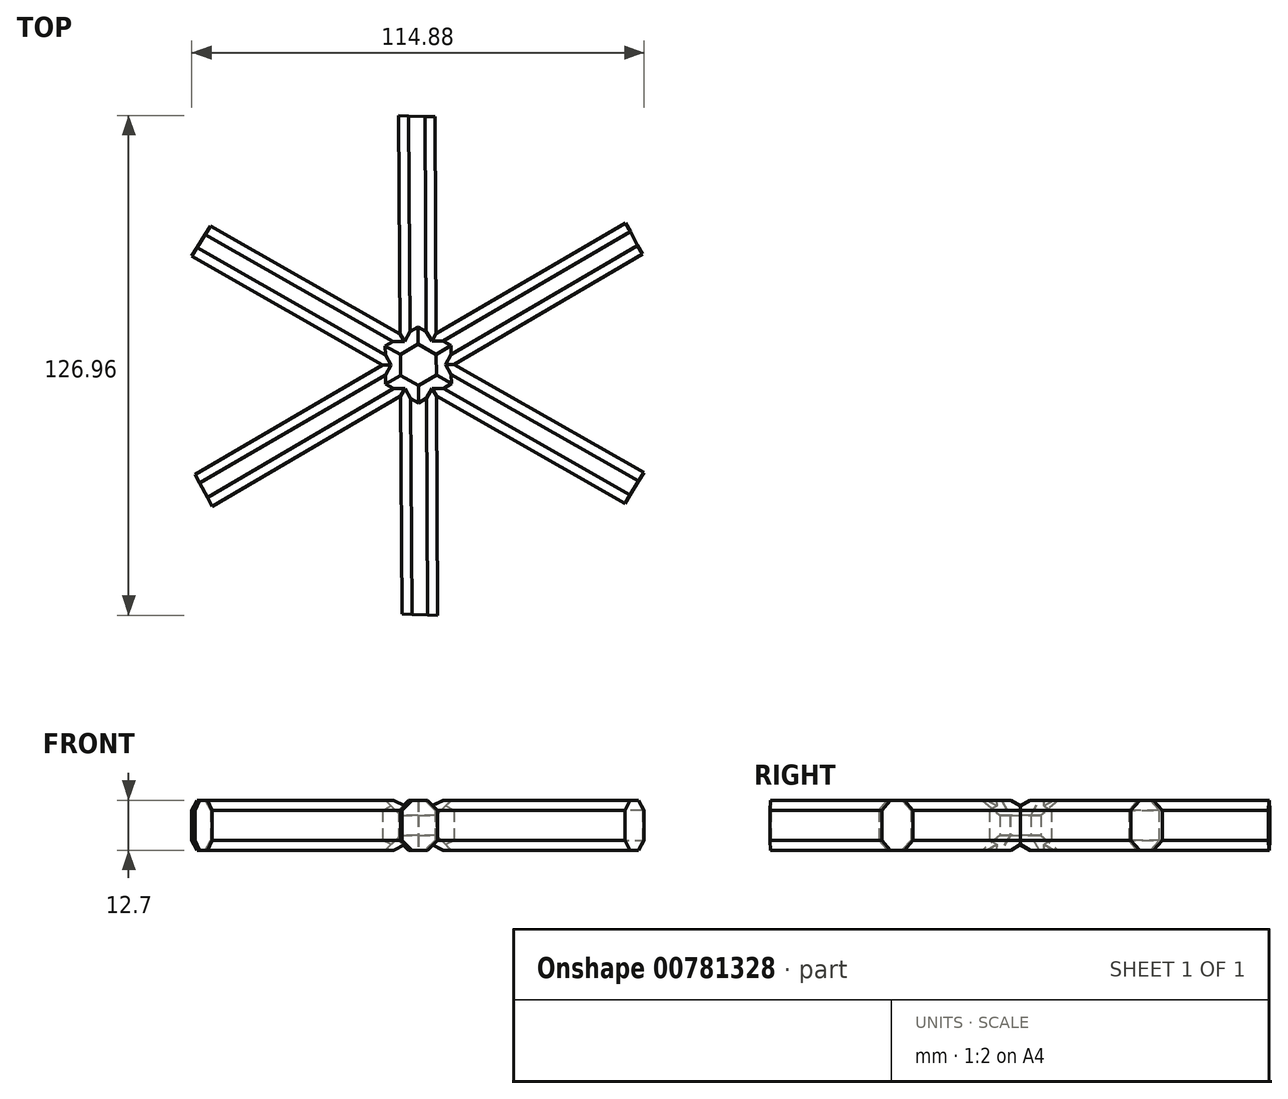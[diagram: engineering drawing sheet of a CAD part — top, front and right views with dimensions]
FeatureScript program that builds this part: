
annotation { "Feature Type Name" : "Feature", "Feature Type Description" : "" }
export const myFeature = defineFeature(function(context is Context, id is Id, definition is map)
    precondition{}
    {
        {
            var Q0;
            Q0=qCreatedBy(makeId("Top.planeOp"),FACE);
            var sketch = newSketch(context, id + "F0", { "sketchPlane" : qUnion([Q0])});
            skPoint(sketch, "E0.center", {"position": v(0, 0) * mm});
            skLineSegment(sketch, "E1", {"start": v(-5, 63.32) * mm, "end": v(-4.1, -63.34) * mm});
            skLineSegment(sketch, "E2", {"start": v(4.25, 63.02) * mm, "end": v(4.87, -63.64) * mm});
            skLineSegment(sketch, "E3.1.2", {"start": v(-52.34, -35.98) * mm, "end": v(56.9, 28.12) * mm});
            skLineSegment(sketch, "E3.1.3", {"start": v(-56.7, -27.83) * mm, "end": v(52.68, 36.04) * mm});
            skLineSegment(sketch, "E3.2.2", {"start": v(57.33, -27.33) * mm, "end": v(-52.8, 35.22) * mm});
            skLineSegment(sketch, "E3.2.3", {"start": v(52.45, -35.2) * mm, "end": v(-57.55, 27.6) * mm});
            skLineSegment(sketch, "E4", {"start": v(4.25, 63.02) * mm, "end": v(-5, 63.32) * mm});
            skLineSegment(sketch, "E5", {"start": v(-52.8, 35.22) * mm, "end": v(-57.55, 27.6) * mm});
            skLineSegment(sketch, "E6", {"start": v(-52.34, -35.98) * mm, "end": v(-56.7, -27.83) * mm});
            skLineSegment(sketch, "E7", {"start": v(-4.1, -63.34) * mm, "end": v(4.87, -63.64) * mm});
            skLineSegment(sketch, "E8", {"start": v(52.45, -35.2) * mm, "end": v(57.33, -27.33) * mm});
            skLineSegment(sketch, "E9", {"start": v(56.9, 28.12) * mm, "end": v(52.68, 36.04) * mm});
            skSolve(sketch);
        }
        {
            var Q0;
            Q0 = qSketchRegion(id + "F0", true);
            extrude(context, id + "F1", {"entities" : qUnion([Q0]), "depth" : 12.7 * mm, "offsetDistance" : 25.4 * mm});
        }
        {
            var Q0;
            {var subQ0=sQuery(id+"F0.wireOp",EDGE,"E3.1.2");Q0=makeQuery(id+"F1.opExtrude","CAP_EDGE",EDGE,{"disambiguationData":[OSD([subQ0]),TDD([makeQuery(id+"F0.imprint","IMPRINT",EDGE,{"disambiguationData":[TD([[makeQuery(id+"F0.imprint","INTERSECT",VERTEX,{"derivedFrom":[sQuery(id+"F0.wireOp",EDGE,"E2"),subQ0]}),1.0]])],"derivedFrom":subQ0})])],"isStart":false});}
            var Q1;
            {var subQ0=sQuery(id+"F0.wireOp",EDGE,"E3.2.3");Q1=makeQuery(id+"F1.opExtrude","CAP_EDGE",EDGE,{"disambiguationData":[OSD([subQ0]),TDD([makeQuery(id+"F0.imprint","IMPRINT",EDGE,{"disambiguationData":[TD([[makeQuery(id+"F0.imprint","INTERSECT",VERTEX,{"derivedFrom":[sQuery(id+"F0.wireOp",EDGE,"E1"),subQ0]}),1.0]])],"derivedFrom":subQ0})])],"isStart":false});}
            var Q2;
            {var subQ0=sQuery(id+"F0.wireOp",EDGE,"E1");Q2=makeQuery(id+"F1.opExtrude","CAP_EDGE",EDGE,{"disambiguationData":[OSD([subQ0]),TDD([makeQuery(id+"F0.imprint","IMPRINT",EDGE,{"disambiguationData":[TD([[makeQuery(id+"F0.imprint","INTERSECT",VERTEX,{"derivedFrom":[subQ0,sQuery(id+"F0.wireOp",EDGE,"E3.1.3")]}),-1.0]])],"derivedFrom":subQ0})])],"isStart":false});}
            var Q3;
            {var subQ0=sQuery(id+"F0.wireOp",EDGE,"E3.1.3");Q3=makeQuery(id+"F1.opExtrude","CAP_EDGE",EDGE,{"disambiguationData":[OSD([subQ0]),TDD([makeQuery(id+"F0.imprint","IMPRINT",EDGE,{"disambiguationData":[TD([[makeQuery(id+"F0.imprint","INTERSECT",VERTEX,{"derivedFrom":[sQuery(id+"F0.wireOp",EDGE,"E1"),subQ0]}),-1.0]])],"derivedFrom":subQ0})])],"isStart":false});}
            var Q4;
            {var subQ0=sQuery(id+"F0.wireOp",EDGE,"E3.2.2");Q4=makeQuery(id+"F1.opExtrude","CAP_EDGE",EDGE,{"disambiguationData":[OSD([subQ0]),TDD([makeQuery(id+"F0.imprint","IMPRINT",EDGE,{"disambiguationData":[TD([[makeQuery(id+"F0.imprint","INTERSECT",VERTEX,{"derivedFrom":[sQuery(id+"F0.wireOp",EDGE,"E2"),subQ0]}),-1.0]])],"derivedFrom":subQ0})])],"isStart":false});}
            var Q5;
            {var subQ0=sQuery(id+"F0.wireOp",EDGE,"E2");Q5=makeQuery(id+"F1.opExtrude","CAP_EDGE",EDGE,{"disambiguationData":[OSD([subQ0]),TDD([makeQuery(id+"F0.imprint","IMPRINT",EDGE,{"disambiguationData":[TD([[makeQuery(id+"F0.imprint","INTERSECT",VERTEX,{"derivedFrom":[subQ0,sQuery(id+"F0.wireOp",EDGE,"E3.2.2")]}),-1.0]])],"derivedFrom":subQ0})])],"isStart":false});}
            var Q6;
            {var subQ0=sQuery(id+"F0.wireOp",EDGE,"E3.2.3");Q6=makeQuery(id+"F1.opExtrude","CAP_EDGE",EDGE,{"disambiguationData":[OSD([subQ0]),TDD([makeQuery(id+"F0.imprint","IMPRINT",EDGE,{"disambiguationData":[TD([[makeQuery(id+"F0.imprint","INTERSECT",VERTEX,{"derivedFrom":[sQuery(id+"F0.wireOp",EDGE,"E1"),subQ0]}),1.0]])],"derivedFrom":subQ0})])],"isStart":true});}
            var Q7;
            {var subQ0=sQuery(id+"F0.wireOp",EDGE,"E3.1.2");Q7=makeQuery(id+"F1.opExtrude","CAP_EDGE",EDGE,{"disambiguationData":[OSD([subQ0]),TDD([makeQuery(id+"F0.imprint","IMPRINT",EDGE,{"disambiguationData":[TD([[makeQuery(id+"F0.imprint","INTERSECT",VERTEX,{"derivedFrom":[sQuery(id+"F0.wireOp",EDGE,"E2"),subQ0]}),1.0]])],"derivedFrom":subQ0})])],"isStart":true});}
            var Q8;
            {var subQ0=sQuery(id+"F0.wireOp",EDGE,"E2");Q8=makeQuery(id+"F1.opExtrude","CAP_EDGE",EDGE,{"disambiguationData":[OSD([subQ0]),TDD([makeQuery(id+"F0.imprint","IMPRINT",EDGE,{"disambiguationData":[TD([[makeQuery(id+"F0.imprint","INTERSECT",VERTEX,{"derivedFrom":[subQ0,sQuery(id+"F0.wireOp",EDGE,"E3.2.2")]}),-1.0]])],"derivedFrom":subQ0})])],"isStart":true});}
            var Q9;
            {var subQ0=sQuery(id+"F0.wireOp",EDGE,"E3.2.2");Q9=makeQuery(id+"F1.opExtrude","CAP_EDGE",EDGE,{"disambiguationData":[OSD([subQ0]),TDD([makeQuery(id+"F0.imprint","IMPRINT",EDGE,{"disambiguationData":[TD([[makeQuery(id+"F0.imprint","INTERSECT",VERTEX,{"derivedFrom":[sQuery(id+"F0.wireOp",EDGE,"E2"),subQ0]}),-1.0]])],"derivedFrom":subQ0})])],"isStart":true});}
            var Q10;
            {var subQ0=sQuery(id+"F0.wireOp",EDGE,"E3.1.3");Q10=makeQuery(id+"F1.opExtrude","CAP_EDGE",EDGE,{"disambiguationData":[OSD([subQ0]),TDD([makeQuery(id+"F0.imprint","IMPRINT",EDGE,{"disambiguationData":[TD([[makeQuery(id+"F0.imprint","INTERSECT",VERTEX,{"derivedFrom":[sQuery(id+"F0.wireOp",EDGE,"E1"),subQ0]}),-1.0]])],"derivedFrom":subQ0})])],"isStart":true});}
            var Q11;
            {var subQ0=sQuery(id+"F0.wireOp",EDGE,"E1");Q11=makeQuery(id+"F1.opExtrude","CAP_EDGE",EDGE,{"disambiguationData":[OSD([subQ0]),TDD([makeQuery(id+"F0.imprint","IMPRINT",EDGE,{"disambiguationData":[TD([[makeQuery(id+"F0.imprint","INTERSECT",VERTEX,{"derivedFrom":[subQ0,sQuery(id+"F0.wireOp",EDGE,"E3.1.3")]}),-1.0]])],"derivedFrom":subQ0})])],"isStart":true});}
            chamfer(context, id + "F2", {"entities" : qUnion([Q0, Q1, Q2, Q3, Q4, Q5, Q6, Q7, Q8, Q9, Q10, Q11]), "width" : 3.8 * mm, "tangentPropagation" : true});
        }
        {
            var Q0;
            {var subQ0=sQuery(id+"F0.wireOp",EDGE,"E3.1.3");Q0=makeQuery(id+"F1.opExtrude","CAP_EDGE",EDGE,{"disambiguationData":[OSD([subQ0]),TDD([makeQuery(id+"F0.imprint","IMPRINT",EDGE,{"disambiguationData":[TD([[makeQuery(id+"F0.imprint","INTERSECT",VERTEX,{"derivedFrom":[sQuery(id+"F0.wireOp",EDGE,"E3.1.1"),subQ0]}),-1.0]])],"derivedFrom":subQ0})])],"isStart":false});}
            var Q1;
            {var subQ0=sQuery(id+"F0.wireOp",EDGE,"E3.1.2");Q1=makeQuery(id+"F1.opExtrude","CAP_EDGE",EDGE,{"disambiguationData":[OSD([subQ0]),TDD([makeQuery(id+"F0.imprint","IMPRINT",EDGE,{"disambiguationData":[TD([[makeQuery(id+"F0.imprint","INTERSECT",VERTEX,{"derivedFrom":[sQuery(id+"F0.wireOp",EDGE,"E3.1.0"),subQ0]}),-1.0]])],"derivedFrom":subQ0})])],"isStart":false});}
            var Q2;
            {var subQ0=sQuery(id+"F0.wireOp",EDGE,"E1");Q2=makeQuery(id+"F1.opExtrude","CAP_EDGE",EDGE,{"disambiguationData":[OSD([subQ0]),TDD([makeQuery(id+"F0.imprint","IMPRINT",EDGE,{"disambiguationData":[TD([[makeQuery(id+"F0.imprint","INTERSECT",VERTEX,{"derivedFrom":[sQuery(id+"F0.wireOp",EDGE,"0ec2d1ad-9409-4326-b42b-d501e9a67073.2.1"),subQ0]}),1.0]])],"derivedFrom":subQ0})])],"isStart":false});}
            var Q3;
            {var subQ0=sQuery(id+"F0.wireOp",EDGE,"E2");Q3=makeQuery(id+"F1.opExtrude","CAP_EDGE",EDGE,{"disambiguationData":[OSD([subQ0]),TDD([makeQuery(id+"F0.imprint","IMPRINT",EDGE,{"disambiguationData":[TD([[makeQuery(id+"F0.imprint","INTERSECT",VERTEX,{"derivedFrom":[sQuery(id+"F0.wireOp",EDGE,"0ec2d1ad-9409-4326-b42b-d501e9a67073.2.0"),subQ0]}),1.0]])],"derivedFrom":subQ0})])],"isStart":false});}
            var Q4;
            {var subQ0=sQuery(id+"F0.wireOp",EDGE,"E3.2.3");Q4=makeQuery(id+"F1.opExtrude","CAP_EDGE",EDGE,{"disambiguationData":[OSD([subQ0]),TDD([makeQuery(id+"F0.imprint","IMPRINT",EDGE,{"disambiguationData":[TD([[makeQuery(id+"F0.imprint","INTERSECT",VERTEX,{"derivedFrom":[sQuery(id+"F0.wireOp",EDGE,"E3.2.1"),subQ0]}),-1.0]])],"derivedFrom":subQ0})])],"isStart":false});}
            var Q5;
            {var subQ0=sQuery(id+"F0.wireOp",EDGE,"E3.2.2");Q5=makeQuery(id+"F1.opExtrude","CAP_EDGE",EDGE,{"disambiguationData":[OSD([subQ0]),TDD([makeQuery(id+"F0.imprint","IMPRINT",EDGE,{"disambiguationData":[TD([[makeQuery(id+"F0.imprint","INTERSECT",VERTEX,{"derivedFrom":[sQuery(id+"F0.wireOp",EDGE,"E3.2.0"),subQ0]}),-1.0]])],"derivedFrom":subQ0})])],"isStart":false});}
            var Q6;
            {var subQ0=sQuery(id+"F0.wireOp",EDGE,"E3.1.2");Q6=makeQuery(id+"F1.opExtrude","CAP_EDGE",EDGE,{"disambiguationData":[OSD([subQ0]),TDD([makeQuery(id+"F0.imprint","IMPRINT",EDGE,{"disambiguationData":[TD([[makeQuery(id+"F0.imprint","INTERSECT",VERTEX,{"derivedFrom":[subQ0,sQuery(id+"F0.wireOp",EDGE,"E3.1.4")]}),1.0]])],"derivedFrom":subQ0})])],"isStart":false});}
            var Q7;
            {var subQ0=sQuery(id+"F0.wireOp",EDGE,"E3.1.3");Q7=makeQuery(id+"F1.opExtrude","CAP_EDGE",EDGE,{"disambiguationData":[OSD([subQ0]),TDD([makeQuery(id+"F0.imprint","IMPRINT",EDGE,{"disambiguationData":[TD([[makeQuery(id+"F0.imprint","INTERSECT",VERTEX,{"derivedFrom":[subQ0,sQuery(id+"F0.wireOp",EDGE,"E3.1.5")]}),1.0]])],"derivedFrom":subQ0})])],"isStart":false});}
            var Q8;
            {var subQ0=sQuery(id+"F0.wireOp",EDGE,"E2");Q8=makeQuery(id+"F1.opExtrude","CAP_EDGE",EDGE,{"disambiguationData":[OSD([subQ0]),TDD([makeQuery(id+"F0.imprint","IMPRINT",EDGE,{"disambiguationData":[TD([[makeQuery(id+"F0.imprint","INTERSECT",VERTEX,{"derivedFrom":[sQuery(id+"F0.wireOp",EDGE,"ff8WDoxF-0HNN-nmSW-Kfdg-EadSLhgNuP1g"),subQ0]}),-1.0]])],"derivedFrom":subQ0})])],"isStart":false});}
            var Q9;
            {var subQ0=sQuery(id+"F0.wireOp",EDGE,"E1");Q9=makeQuery(id+"F1.opExtrude","CAP_EDGE",EDGE,{"disambiguationData":[OSD([subQ0]),TDD([makeQuery(id+"F0.imprint","IMPRINT",EDGE,{"disambiguationData":[TD([[makeQuery(id+"F0.imprint","INTERSECT",VERTEX,{"derivedFrom":[sQuery(id+"F0.wireOp",EDGE,"zlb1Aynz-YbEw-ficQ-rFmi-VnWJ8KB2Ca5n"),subQ0]}),-1.0]])],"derivedFrom":subQ0})])],"isStart":false});}
            var Q10;
            {var subQ0=sQuery(id+"F0.wireOp",EDGE,"E3.2.2");Q10=makeQuery(id+"F1.opExtrude","CAP_EDGE",EDGE,{"disambiguationData":[OSD([subQ0]),TDD([makeQuery(id+"F0.imprint","IMPRINT",EDGE,{"disambiguationData":[TD([[makeQuery(id+"F0.imprint","INTERSECT",VERTEX,{"derivedFrom":[subQ0,sQuery(id+"F0.wireOp",EDGE,"E3.2.4")]}),1.0]])],"derivedFrom":subQ0})])],"isStart":false});}
            var Q11;
            {var subQ0=sQuery(id+"F0.wireOp",EDGE,"E3.2.3");Q11=makeQuery(id+"F1.opExtrude","CAP_EDGE",EDGE,{"disambiguationData":[OSD([subQ0]),TDD([makeQuery(id+"F0.imprint","IMPRINT",EDGE,{"disambiguationData":[TD([[makeQuery(id+"F0.imprint","INTERSECT",VERTEX,{"derivedFrom":[subQ0,sQuery(id+"F0.wireOp",EDGE,"E3.2.5")]}),1.0]])],"derivedFrom":subQ0})])],"isStart":false});}
            var Q12;
            {var subQ0=sQuery(id+"F0.wireOp",EDGE,"E3.1.3");Q12=makeQuery(id+"F1.opExtrude","CAP_EDGE",EDGE,{"disambiguationData":[OSD([subQ0]),TDD([makeQuery(id+"F0.imprint","IMPRINT",EDGE,{"disambiguationData":[TD([[makeQuery(id+"F0.imprint","INTERSECT",VERTEX,{"derivedFrom":[sQuery(id+"F0.wireOp",EDGE,"E3.1.1"),subQ0]}),-1.0]])],"derivedFrom":subQ0})])],"isStart":true});}
            var Q13;
            {var subQ0=sQuery(id+"F0.wireOp",EDGE,"E3.1.2");Q13=makeQuery(id+"F1.opExtrude","CAP_EDGE",EDGE,{"disambiguationData":[OSD([subQ0]),TDD([makeQuery(id+"F0.imprint","IMPRINT",EDGE,{"disambiguationData":[TD([[makeQuery(id+"F0.imprint","INTERSECT",VERTEX,{"derivedFrom":[sQuery(id+"F0.wireOp",EDGE,"E3.1.0"),subQ0]}),-1.0]])],"derivedFrom":subQ0})])],"isStart":true});}
            var Q14;
            {var subQ0=sQuery(id+"F0.wireOp",EDGE,"E1");Q14=makeQuery(id+"F1.opExtrude","CAP_EDGE",EDGE,{"disambiguationData":[OSD([subQ0]),TDD([makeQuery(id+"F0.imprint","IMPRINT",EDGE,{"disambiguationData":[TD([[makeQuery(id+"F0.imprint","INTERSECT",VERTEX,{"derivedFrom":[sQuery(id+"F0.wireOp",EDGE,"0ec2d1ad-9409-4326-b42b-d501e9a67073.2.1"),subQ0]}),1.0]])],"derivedFrom":subQ0})])],"isStart":true});}
            var Q15;
            {var subQ0=sQuery(id+"F0.wireOp",EDGE,"E2");Q15=makeQuery(id+"F1.opExtrude","CAP_EDGE",EDGE,{"disambiguationData":[OSD([subQ0]),TDD([makeQuery(id+"F0.imprint","IMPRINT",EDGE,{"disambiguationData":[TD([[makeQuery(id+"F0.imprint","INTERSECT",VERTEX,{"derivedFrom":[sQuery(id+"F0.wireOp",EDGE,"0ec2d1ad-9409-4326-b42b-d501e9a67073.2.0"),subQ0]}),1.0]])],"derivedFrom":subQ0})])],"isStart":true});}
            var Q16;
            {var subQ0=sQuery(id+"F0.wireOp",EDGE,"E3.2.3");Q16=makeQuery(id+"F1.opExtrude","CAP_EDGE",EDGE,{"disambiguationData":[OSD([subQ0]),TDD([makeQuery(id+"F0.imprint","IMPRINT",EDGE,{"disambiguationData":[TD([[makeQuery(id+"F0.imprint","INTERSECT",VERTEX,{"derivedFrom":[sQuery(id+"F0.wireOp",EDGE,"E3.2.1"),subQ0]}),-1.0]])],"derivedFrom":subQ0})])],"isStart":true});}
            var Q17;
            {var subQ0=sQuery(id+"F0.wireOp",EDGE,"E3.2.2");Q17=makeQuery(id+"F1.opExtrude","CAP_EDGE",EDGE,{"disambiguationData":[OSD([subQ0]),TDD([makeQuery(id+"F0.imprint","IMPRINT",EDGE,{"disambiguationData":[TD([[makeQuery(id+"F0.imprint","INTERSECT",VERTEX,{"derivedFrom":[sQuery(id+"F0.wireOp",EDGE,"E3.2.0"),subQ0]}),-1.0]])],"derivedFrom":subQ0})])],"isStart":true});}
            var Q18;
            {var subQ0=sQuery(id+"F0.wireOp",EDGE,"E3.1.2");Q18=makeQuery(id+"F1.opExtrude","CAP_EDGE",EDGE,{"disambiguationData":[OSD([subQ0]),TDD([makeQuery(id+"F0.imprint","IMPRINT",EDGE,{"disambiguationData":[TD([[makeQuery(id+"F0.imprint","INTERSECT",VERTEX,{"derivedFrom":[subQ0,sQuery(id+"F0.wireOp",EDGE,"E3.1.4")]}),1.0]])],"derivedFrom":subQ0})])],"isStart":true});}
            var Q19;
            {var subQ0=sQuery(id+"F0.wireOp",EDGE,"E3.1.3");Q19=makeQuery(id+"F1.opExtrude","CAP_EDGE",EDGE,{"disambiguationData":[OSD([subQ0]),TDD([makeQuery(id+"F0.imprint","IMPRINT",EDGE,{"disambiguationData":[TD([[makeQuery(id+"F0.imprint","INTERSECT",VERTEX,{"derivedFrom":[subQ0,sQuery(id+"F0.wireOp",EDGE,"E3.1.5")]}),1.0]])],"derivedFrom":subQ0})])],"isStart":true});}
            var Q20;
            {var subQ0=sQuery(id+"F0.wireOp",EDGE,"E3.2.3");Q20=makeQuery(id+"F1.opExtrude","CAP_EDGE",EDGE,{"disambiguationData":[OSD([subQ0]),TDD([makeQuery(id+"F0.imprint","IMPRINT",EDGE,{"disambiguationData":[TD([[makeQuery(id+"F0.imprint","INTERSECT",VERTEX,{"derivedFrom":[subQ0,sQuery(id+"F0.wireOp",EDGE,"E3.2.5")]}),1.0]])],"derivedFrom":subQ0})])],"isStart":true});}
            var Q21;
            {var subQ0=sQuery(id+"F0.wireOp",EDGE,"E3.2.2");Q21=makeQuery(id+"F1.opExtrude","CAP_EDGE",EDGE,{"disambiguationData":[OSD([subQ0]),TDD([makeQuery(id+"F0.imprint","IMPRINT",EDGE,{"disambiguationData":[TD([[makeQuery(id+"F0.imprint","INTERSECT",VERTEX,{"derivedFrom":[subQ0,sQuery(id+"F0.wireOp",EDGE,"E3.2.4")]}),1.0]])],"derivedFrom":subQ0})])],"isStart":true});}
            var Q22;
            {var subQ0=sQuery(id+"F0.wireOp",EDGE,"E2");Q22=makeQuery(id+"F1.opExtrude","CAP_EDGE",EDGE,{"disambiguationData":[OSD([subQ0]),TDD([makeQuery(id+"F0.imprint","IMPRINT",EDGE,{"disambiguationData":[TD([[makeQuery(id+"F0.imprint","INTERSECT",VERTEX,{"derivedFrom":[sQuery(id+"F0.wireOp",EDGE,"ff8WDoxF-0HNN-nmSW-Kfdg-EadSLhgNuP1g"),subQ0]}),-1.0]])],"derivedFrom":subQ0})])],"isStart":true});}
            var Q23;
            {var subQ0=sQuery(id+"F0.wireOp",EDGE,"E1");Q23=makeQuery(id+"F1.opExtrude","CAP_EDGE",EDGE,{"disambiguationData":[OSD([subQ0]),TDD([makeQuery(id+"F0.imprint","IMPRINT",EDGE,{"disambiguationData":[TD([[makeQuery(id+"F0.imprint","INTERSECT",VERTEX,{"derivedFrom":[sQuery(id+"F0.wireOp",EDGE,"zlb1Aynz-YbEw-ficQ-rFmi-VnWJ8KB2Ca5n"),subQ0]}),-1.0]])],"derivedFrom":subQ0})])],"isStart":true});}
            chamfer(context, id + "F3", {"entities" : qUnion([Q0, Q1, Q2, Q3, Q4, Q5, Q6, Q7, Q8, Q9, Q10, Q11, Q12, Q13, Q14, Q15, Q16, Q17, Q18, Q19, Q20, Q21, Q22, Q23]), "chamferType" : ChamferType.TWO_OFFSETS, "width1" : 2.54 * mm, "oppositeDirection" : false, "width2" : 2.54 * mm, "tangentPropagation" : true});
        }
    });
